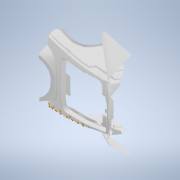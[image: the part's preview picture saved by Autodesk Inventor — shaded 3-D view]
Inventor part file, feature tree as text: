
AUTODESK INVENTOR PART (.ipt)
format: ipt  version: 2021 (Build 250183000, 183)  size: 13,628,416 bytes
history: native  units: mm
features: other x53, sketch x1, loft x1
ambient origin geometry x8: Origin, YZ Plane, XZ Plane, XY Plane, X Axis, Y Axis, Z Axis, Center Point
bodies: Body1 (feature_tree)
feature tree (55):
  other  "WaveRunner_GloveBox"
  other  "Work Point1"
  other  "Work Point2"
  other  "Work Point3"
  other  "Work Point4"
  other  "Work Point5"
  other  "Work Point6"
  other  "Work Point7"
  other  "Work Point8"
  other  "Work Point9"
  other  "Work Point10"
  other  "Work Point11"
  other  "Work Point12"
  other  "Work Point13"
  other  "Work Point14"
  other  "Work Point15"
  other  "Work Point16"
  other  "Work Point17"
  other  "Work Point18"
  other  "Work Point19"
  other  "Work Point20"
  other  "Work Point21"
  other  "Work Point22"
  other  "Work Point23"
  other  "Work Point24"
  other  "Work Point25"
  other  "Work Point26"
  other  "Work Point27"
  other  "Work Point28"
  other  "Work Point29"
  other  "Work Point30"
  other  "Work Point31"
  other  "Work Point32"
  other  "Work Point33"
  other  "Work Point34"
  other  "Work Point35"
  other  "Work Point36"
  other  "Work Point37"
  other  "Work Point38"
  other  "Work Point39"
  other  "Work Point40"
  other  "Work Point41"
  other  "Work Point42"
  other  "Work Point43"
  other  "Work Point44"
  other  "Work Point45"
  other  "Work Point46"
  other  "Work Point47"
  other  "Work Point48"
  other  "Work Point49"
  other  "Work Point50"
  sketch  "3D Sketch2"
  other  "Srf2"
  loft  "LoftSrf2"
  other  "WaveRunner_GloveBox.obj"
